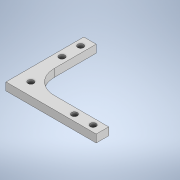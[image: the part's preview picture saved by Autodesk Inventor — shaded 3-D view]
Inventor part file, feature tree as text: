
AUTODESK INVENTOR PART (.ipt)
format: ipt  version: 2021 (Build 250183000, 183)  size: 116,736 bytes
history: native  units: mm
features: sketch x1, extrude x1, hole x1
ambient origin geometry x8: Origin, YZ Plane, XZ Plane, XY Plane, X Axis, Y Axis, Z Axis, Center Point
bodies: Solid1 (feature_tree)
feature tree (3):
  sketch  "Sketch1"  dims[d0=58.0mm d1=50.0mm d2=50.0mm d3=42.0mm d4=15.0mm d5=6.0mm d6=18.0mm d7=18.0mm d8=6.0mm d9=5.0mm d10=0.0mm d11=3.8mm d12=6.0mm d13=4.0mm d14=2.0mm d15=90.0deg d16=8.0mm d17=20.594885mm]
  extrude  "Extrusion1"  Depth=50.0mm
  hole  "Hole1"  [1 undecoded]
note: 1 required parameter value undecoded (feature->parameter linkage not recoverable at this tier; creation-order binding heuristic only, values carry confidence <= 0.55)
